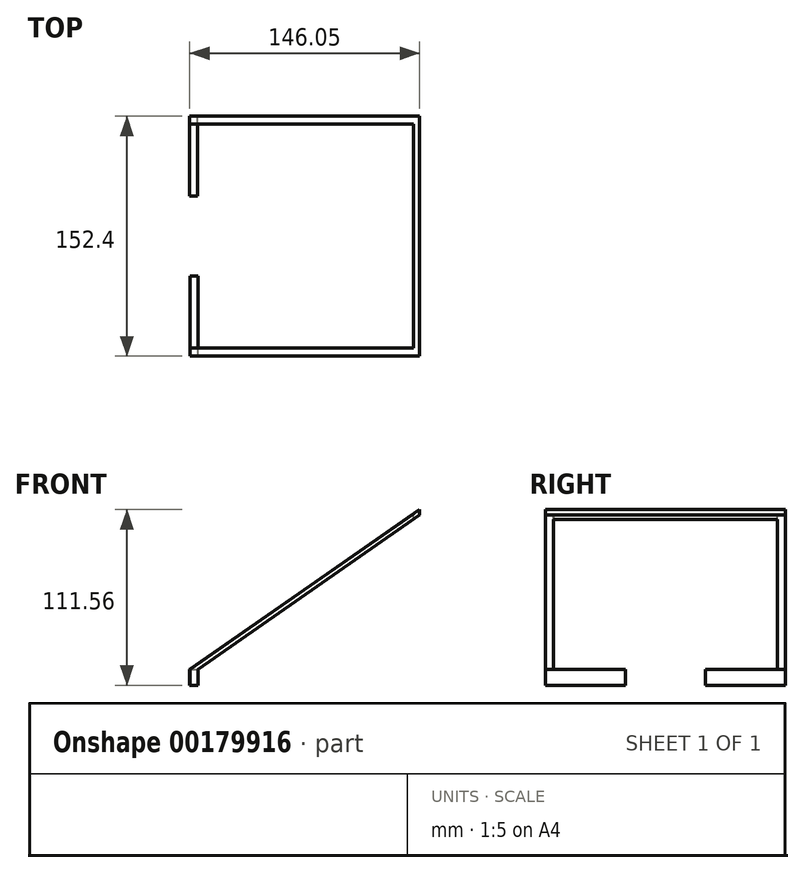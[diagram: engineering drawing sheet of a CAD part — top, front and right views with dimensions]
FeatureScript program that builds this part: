
annotation { "Feature Type Name" : "Feature", "Feature Type Description" : "" }
export const myFeature = defineFeature(function(context is Context, id is Id, definition is map)
    precondition{}
    {
        {
            var Q0;
            Q0=qCreatedBy(makeId("Front.planeOp"),FACE);
            var sketch = newSketch(context, id + "F0", { "sketchPlane" : qUnion([Q0])});
            skLineSegment(sketch, "E0", {"start": v(-30.8, 0) * mm, "end": v(-30.8, -10.16) * mm});
            skLineSegment(sketch, "E1", {"start": v(-30.8, 0) * mm, "end": v(115.26, 101.4) * mm});
            skLineSegment(sketch, "E2", {"start": v(-30.8, -10.16) * mm, "end": v(-25.71, -10.16) * mm});
            skLineSegment(sketch, "E3", {"start": v(-25.71, -10.16) * mm, "end": v(-25.71, 0) * mm});
            skLineSegment(sketch, "E4", {"start": v(-25.71, 0) * mm, "end": v(115.26, 97.87) * mm});
            skLineSegment(sketch, "E5", {"start": v(115.26, 97.87) * mm, "end": v(115.26, 101.4) * mm});
            skSolve(sketch);
        }
        {
            var Q0;
            Q0=makeQuery(id+"F0.imprint","IMPRINT",FACE,{"disambiguationData":[TD([[makeQuery(id+"F0.imprint","IMPRINT",EDGE,{"derivedFrom":sQuery(id+"F0.wireOp",EDGE,"E0")}),1.0]])]});
            extrude(context, id + "F1", {"entities" : qUnion([Q0]), "depth" : 5.08 * mm});
        }
        {
            var Q0;
            Q0=makeQuery(id+"F1.opExtrude","CAP_FACE",FACE,{"disambiguationData":[OSD([sQuery(id+"F0.wireOp",EDGE,"E0"),sQuery(id+"F0.wireOp",EDGE,"E1"),sQuery(id+"F0.wireOp",EDGE,"E2"),sQuery(id+"F0.wireOp",EDGE,"E3"),sQuery(id+"F0.wireOp",EDGE,"E4"),sQuery(id+"F0.wireOp",EDGE,"E5")])],"isStart":false});
            var sketch = newSketch(context, id + "F2", { "sketchPlane" : qUnion([Q0])});
            skLineSegment(sketch, "E6", {"start": v(-30.8, 0) * mm, "end": v(-25.71, 0) * mm});
            skLineSegment(sketch, "E7", {"start": v(-25.71, 0) * mm, "end": v(-25.71, -10.16) * mm});
            skLineSegment(sketch, "E8", {"start": v(-25.71, -10.16) * mm, "end": v(-30.8, -10.16) * mm});
            skLineSegment(sketch, "E9", {"start": v(-30.8, -10.16) * mm, "end": v(-30.8, 0) * mm});
            skLineSegment(sketch, "E10", {"start": v(115.26, 101.4) * mm, "end": v(115.26, 97.87) * mm});
            skLineSegment(sketch, "E11", {"start": v(115.26, 97.87) * mm, "end": v(111.2, 95.06) * mm});
            skLineSegment(sketch, "E12", {"start": v(111.2, 95.06) * mm, "end": v(111.2, 98.59) * mm});
            skLineSegment(sketch, "E13", {"start": v(111.2, 98.59) * mm, "end": v(115.26, 101.4) * mm});
            skSolve(sketch);
        }
        {
            var Q0;
            Q0=makeQuery(id+"F2.imprint","IMPRINT",FACE,{"disambiguationData":[TD([[makeQuery(id+"F2.imprint","IMPRINT",EDGE,{"derivedFrom":sQuery(id+"F2.wireOp",EDGE,"E6")}),-1.0]])]});
            extrude(context, id + "F3", {"entities" : qUnion([Q0]), "operationType" : NewBodyOperationType.ADD, "depth" : 45.72 * mm});
        }
        {
            var Q0;
            Q0=makeQuery(id+"F2.imprint","IMPRINT",FACE,{"disambiguationData":[TD([[makeQuery(id+"F2.imprint","IMPRINT",EDGE,{"derivedFrom":sQuery(id+"F2.wireOp",EDGE,"E10")}),1.0]])]});
            extrude(context, id + "F4", {"entities" : qUnion([Q0]), "operationType" : NewBodyOperationType.ADD, "depth" : 142.24 * mm});
        }
        {
            var Q0;
            Q0=makeQuery(id+"F4.opExtrude","CAP_FACE",FACE,{"disambiguationData":[OSD([sQuery(id+"F2.wireOp",EDGE,"E10"),sQuery(id+"F2.wireOp",EDGE,"E11"),sQuery(id+"F2.wireOp",EDGE,"E12"),sQuery(id+"F2.wireOp",EDGE,"E13")])],"isStart":false});
            var sketch = newSketch(context, id + "F5", { "sketchPlane" : qUnion([Q0])});
            skLineSegment(sketch, "E14", {"start": v(115.26, 101.4) * mm, "end": v(-30.75, 0) * mm});
            skLineSegment(sketch, "E15", {"start": v(-30.75, 0) * mm, "end": v(-30.75, -10.16) * mm});
            skLineSegment(sketch, "E16", {"start": v(-30.75, -10.16) * mm, "end": v(-25.68, -10.16) * mm});
            skLineSegment(sketch, "E17", {"start": v(-25.68, -10.16) * mm, "end": v(-25.68, 0) * mm});
            skLineSegment(sketch, "E18", {"start": v(-25.68, 0) * mm, "end": v(115.26, 97.87) * mm});
            skLineSegment(sketch, "E19", {"start": v(115.26, 97.87) * mm, "end": v(115.26, 101.4) * mm});
            skSolve(sketch);
        }
        {
            var Q0;
            Q0 = qSketchRegion(id + "F5", true);
            extrude(context, id + "F6", {"entities" : qUnion([Q0]), "operationType" : NewBodyOperationType.ADD, "depth" : 5.08 * mm});
        }
        {
            var Q0;
            Q0=makeQuery(id+"F6.opExtrude","CAP_FACE",FACE,{"disambiguationData":[OSD([sQuery(id+"F5.wireOp",EDGE,"E14"),sQuery(id+"F5.wireOp",EDGE,"E15"),sQuery(id+"F5.wireOp",EDGE,"E16"),sQuery(id+"F5.wireOp",EDGE,"E17"),sQuery(id+"F5.wireOp",EDGE,"E18"),sQuery(id+"F5.wireOp",EDGE,"E19")])],"isStart":false});
            var sketch = newSketch(context, id + "F7", { "sketchPlane" : qUnion([Q0])});
            skLineSegment(sketch, "E20", {"start": v(-30.75, 0) * mm, "end": v(-25.68, 0) * mm});
            skLineSegment(sketch, "E21", {"start": v(-25.68, 0) * mm, "end": v(-25.68, -10.16) * mm});
            skLineSegment(sketch, "E22", {"start": v(-25.68, -10.16) * mm, "end": v(-30.75, -10.16) * mm});
            skLineSegment(sketch, "E23", {"start": v(-30.75, -10.16) * mm, "end": v(-30.75, 0) * mm});
            skSolve(sketch);
        }
        {
            var Q0;
            Q0 = qSketchRegion(id + "F7", true);
            extrude(context, id + "F8", {"entities" : qUnion([Q0]), "operationType" : NewBodyOperationType.ADD, "oppositeDirection" : true, "depth" : 50.8 * mm});
        }
    });
